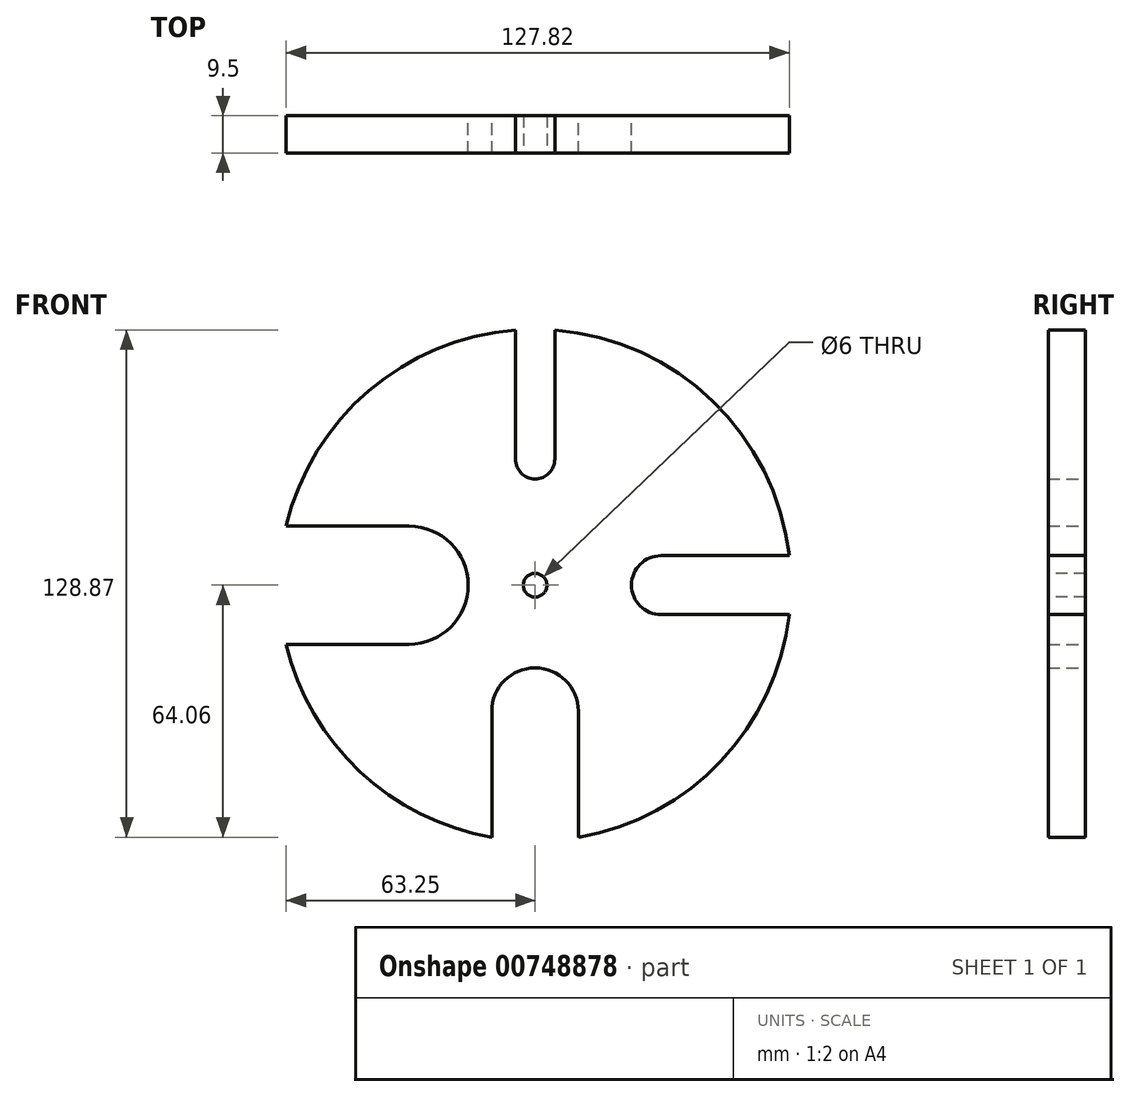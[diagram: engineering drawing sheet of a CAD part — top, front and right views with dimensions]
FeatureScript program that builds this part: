
annotation { "Feature Type Name" : "Feature", "Feature Type Description" : "" }
export const myFeature = defineFeature(function(context is Context, id is Id, definition is map)
    precondition{}
    {
        {
            var Q0;
            Q0=qCreatedBy(makeId("Front.planeOp"),FACE);
            var sketch = newSketch(context, id + "F0", { "sketchPlane" : qUnion([Q0])});
            skArc(sketch, "E0", {"start": v(11, -64.06) * mm, "mid": v(47.2, -44.7) * mm, "end": v(64.57, -7.5) * mm});
            skPoint(sketch, "E1", {"position": v(0, 65) * mm});
            skPoint(sketch, "E2", {"position": v(65, 0) * mm});
            skPoint(sketch, "E3", {"position": v(0, -65) * mm});
            skPoint(sketch, "E4", {"position": v(0, 32) * mm});
            skPoint(sketch, "E5", {"position": v(32, 0) * mm});
            skPoint(sketch, "E6", {"position": v(0, -32) * mm});
            skPoint(sketch, "E7", {"position": v(-32, 0) * mm});
            skArc(sketch, "E8", {"start": v(-5, 32) * mm, "mid": v(0, 27) * mm, "end": v(5, 32) * mm});
            skArc(sketch, "E9", {"start": v(32, 7.5) * mm, "mid": v(24.5, 0) * mm, "end": v(32, -7.5) * mm});
            skArc(sketch, "E10", {"start": v(-32, -15) * mm, "mid": v(-17, 0) * mm, "end": v(-32, 15) * mm});
            skArc(sketch, "E11", {"start": v(11, -32) * mm, "mid": v(0, -21) * mm, "end": v(-11, -32) * mm});
            skLineSegment(sketch, "E12", {"start": v(-5, 32) * mm, "end": v(-5, 65) * mm});
            skLineSegment(sketch, "E13", {"start": v(5, 32) * mm, "end": v(5, 64.8) * mm});
            skLineSegment(sketch, "E14", {"start": v(32, 7.5) * mm, "end": v(64.57, 7.5) * mm});
            skLineSegment(sketch, "E15", {"start": v(32, -7.5) * mm, "end": v(64.57, -7.5) * mm});
            skLineSegment(sketch, "E16", {"start": v(11, -32) * mm, "end": v(11, -64.06) * mm});
            skLineSegment(sketch, "E17", {"start": v(-11, -32) * mm, "end": v(-11, -64.06) * mm});
            skArc(sketch, "E18.trimOffspring", {"start": v(64.57, 7.5) * mm, "mid": v(45.07, 46.84) * mm, "end": v(5, 64.8) * mm});
            skLineSegment(sketch, "E19", {"start": v(-32, 15) * mm, "end": v(-63.25, 15) * mm});
            skLineSegment(sketch, "E20", {"start": v(-32, -15) * mm, "end": v(-63.25, -15) * mm});
            skArc(sketch, "E21.trimOffspring", {"start": v(-63.25, -15) * mm, "mid": v(-44.5, -47.38) * mm, "end": v(-11, -64.06) * mm});
            skArc(sketch, "E22.trimOffspring", {"start": v(-5, 64.8) * mm, "mid": v(-42.24, 49.4) * mm, "end": v(-63.25, 15) * mm});
            skSolve(sketch);
        }
        {
            var Q0;
            Q0 = qSketchRegion(id + "F0", true);
            extrude(context, id + "F1", {"entities" : qUnion([Q0]), "depth" : 9.5 * mm, "offsetDistance" : 25 * mm});
        }
        {
            var Q0;
            Q0=makeQuery(id+"F1.opExtrude","CAP_FACE",FACE,{"disambiguationData":[OSD([sQuery(id+"F0.wireOp",EDGE,"E0"),sQuery(id+"F0.wireOp",EDGE,"E8"),sQuery(id+"F0.wireOp",EDGE,"E9"),sQuery(id+"F0.wireOp",EDGE,"E10"),sQuery(id+"F0.wireOp",EDGE,"E11"),sQuery(id+"F0.wireOp",EDGE,"E12"),sQuery(id+"F0.wireOp",EDGE,"E13"),sQuery(id+"F0.wireOp",EDGE,"E14"),sQuery(id+"F0.wireOp",EDGE,"E15"),sQuery(id+"F0.wireOp",EDGE,"E16"),sQuery(id+"F0.wireOp",EDGE,"E17"),sQuery(id+"F0.wireOp",EDGE,"E18.trimOffspring"),sQuery(id+"F0.wireOp",EDGE,"E19"),sQuery(id+"F0.wireOp",EDGE,"E20"),sQuery(id+"F0.wireOp",EDGE,"E21.trimOffspring"),sQuery(id+"F0.wireOp",EDGE,"E22.trimOffspring")])],"isStart":false});
            var sketch = newSketch(context, id + "F2", { "sketchPlane" : qUnion([Q0])});
            skPoint(sketch, "E23", {"position": v(0, 0) * mm});
            skSolve(sketch);
        }
        {
            var Q0;
            Q0=sQuery(id+"F2.wireOp",VERTEX,"E23");
            var Q1;
            Q1=makeQuery(id+"F1.opExtrude","SWEPT_BODY",BODY,{"disambiguationData":[OSD([sQuery(id+"F0.wireOp",EDGE,"E0"),sQuery(id+"F0.wireOp",EDGE,"E8"),sQuery(id+"F0.wireOp",EDGE,"E9"),sQuery(id+"F0.wireOp",EDGE,"E10"),sQuery(id+"F0.wireOp",EDGE,"E11"),sQuery(id+"F0.wireOp",EDGE,"E12"),sQuery(id+"F0.wireOp",EDGE,"E13"),sQuery(id+"F0.wireOp",EDGE,"E14"),sQuery(id+"F0.wireOp",EDGE,"E15"),sQuery(id+"F0.wireOp",EDGE,"E16"),sQuery(id+"F0.wireOp",EDGE,"E17"),sQuery(id+"F0.wireOp",EDGE,"E18.trimOffspring"),sQuery(id+"F0.wireOp",EDGE,"E19"),sQuery(id+"F0.wireOp",EDGE,"E20"),sQuery(id+"F0.wireOp",EDGE,"E21.trimOffspring"),sQuery(id+"F0.wireOp",EDGE,"E22.trimOffspring")])]});
            hole(context, id + "F3", {"style" : HoleStyle.SIMPLE, "endStyle" : HoleEndStyle.THROUGH, "standardTappedOrClearance" : lookupTablePath({ "standard" : "ISO", "size" : "6", "type" : "Drilled" }), "standardBlindInLast" : lookupTablePath({ "standard" : "ISO", "size" : "6", "type" : "Drilled" }), "holeDiameter" : 6 * mm, "majorDiameter" : 3 * mm, "isTappedThrough" : true, "tappedDepth" : 13.25 * mm, "tapClearance" : 3, "locations" : qUnion([Q0]), "scope" : qUnion([Q1])});
        }
    });
